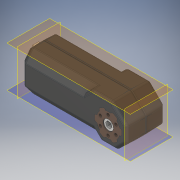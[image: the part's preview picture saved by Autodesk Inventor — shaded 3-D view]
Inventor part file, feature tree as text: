
AUTODESK INVENTOR PART (.ipt)
format: ipt  version: 2017 (Build 210142000, 142)  size: 4,247,040 bytes
history: native  units: in
note: dims shown in document units (in); Inventor stores cm internally (conversion verified against a paired STEP export)
features: other x10, plane x4
ambient origin geometry x8: Origin, YZ Plane, XZ Plane, XY Plane, X Axis, Y Axis, Z Axis, Center Point
bodies: Solid1 (feature_tree), Solid2 (feature_tree), Solid3 (feature_tree), Solid4 (feature_tree), Solid5 (feature_tree), Solid6 (feature_tree), Solid7 (feature_tree), Solid8 (feature_tree)
feature tree (14):
  other  "REV-41-1300HexMotor.ipt"
  other  "Solid1::REV-41-1300HexMotor.ipt"
  other  "Solid2::REV-41-1300HexMotor.ipt"
  other  "Solid3::REV-41-1300HexMotor.ipt"
  other  "Solid4::REV-41-1300HexMotor.ipt"
  other  "Solid5::REV-41-1300HexMotor.ipt"
  other  "Solid6::REV-41-1300HexMotor.ipt"
  other  "Solid7::REV-41-1300HexMotor.ipt"
  other  "Solid8::REV-41-1300HexMotor.ipt"
  other  "TaggingFeature1"
  plane  "Work Plane1"
  plane  "Work Plane2"
  plane  "Work Plane3"
  plane  "Work Plane4"
